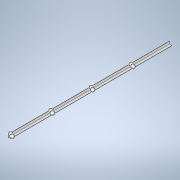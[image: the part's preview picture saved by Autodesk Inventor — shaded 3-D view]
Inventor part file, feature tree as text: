
AUTODESK INVENTOR PART (.ipt)
format: ipt  version: 2020.2 (Build 242310000, 310)  size: 139,264 bytes
history: native  units: in
note: dims shown in document units (in); Inventor stores cm internally (conversion verified against a paired STEP export)
features: sketch x3, hole x2, extrude x1
ambient origin geometry x8: Origin, YZ Plane, XZ Plane, XY Plane, X Axis, Y Axis, Z Axis, Center Point
bodies: Solid1 (feature_tree)
feature tree (6):
  extrude  "Extrusion1"  Depth=0.1181in
  hole  "Hole1"  [1 undecoded]
  hole  "Hole2"  [1 undecoded]
  sketch  "Sketch1"  dims[d0=0.1181in d1=0.1181in]
  sketch  "Sketch2"  dims[d2=1.1811in d3=1.1811in]
  sketch  "Sketch3"  dims[d4=70.8661in d5=0.0in d6=0.5906in d7=0.5906in d8=1.063in d9=0.5906in d10=17.7165in d11=17.7165in d12=0.5906in d13=17.7165in d14=0.5906in d15=0.15in d16=0.2953in d17=0.1476in d18=0.0984in d19=90.0deg d20=0.3937in d21=0.8108in d22=0.5906in d23=0.5906in d24=0.5906in d25=17.7165in d26=17.7165in d27=0.5906in d28=17.7165in d29=0.5906in d30=0.15in d31=0.2953in d32=0.1476in d33=0.0984in d34=90.0deg d35=0.3937in d36=0.8108in d37=0.0in d38=0.0in d39=0.0in d40=0.0in d41=0.0in d42=0.0in d43=0.0in d44=0.0in]
note: 2 required parameter values undecoded (feature->parameter linkage not recoverable at this tier; creation-order binding heuristic only, values carry confidence <= 0.55)
